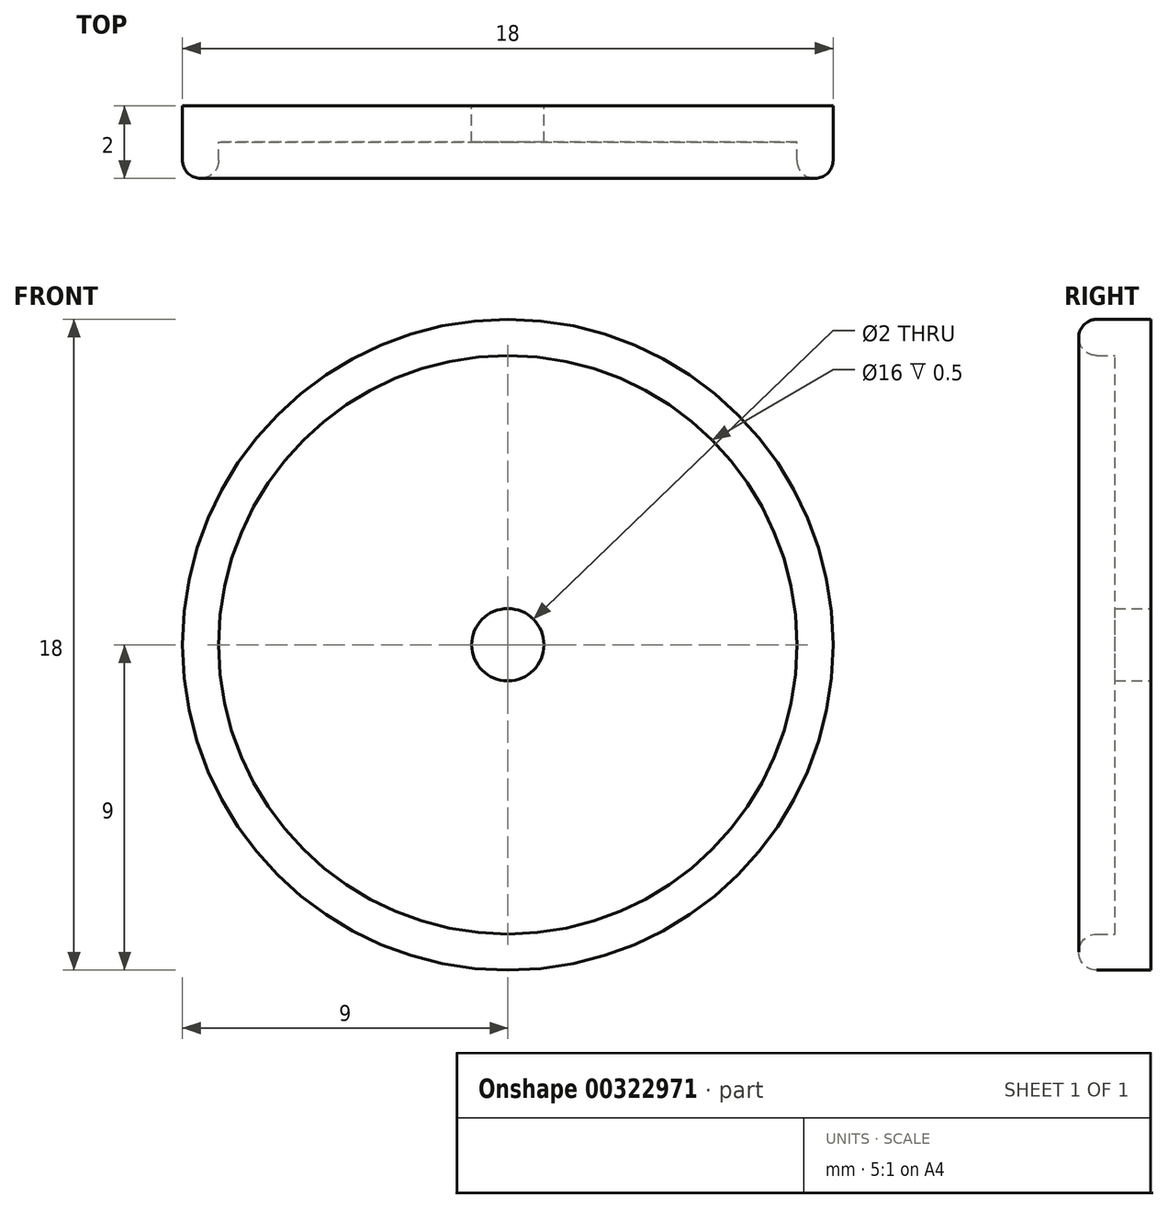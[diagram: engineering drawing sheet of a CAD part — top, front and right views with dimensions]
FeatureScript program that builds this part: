
annotation { "Feature Type Name" : "Feature", "Feature Type Description" : "" }
export const myFeature = defineFeature(function(context is Context, id is Id, definition is map)
    precondition{}
    {
        {
            var Q0;
            Q0=qCreatedBy(makeId("Front.planeOp"),FACE);
            var sketch = newSketch(context, id + "F0", { "sketchPlane" : qUnion([Q0])});
            skCircle(sketch, "E0", {"center": v(0, 0) * mm, "radius": 1 * mm});
            skCircle(sketch, "E1", {"center": v(0, 0) * mm, "radius": 9 * mm});
            skCircle(sketch, "E2", {"center": v(0, 0) * mm, "radius": 8 * mm});
            skSolve(sketch);
        }
        {
            var Q0;
            Q0=makeQuery(id+"F0.imprint","IMPRINT",FACE,{"disambiguationData":[TD([[makeQuery(id+"F0.imprint","IMPRINT",EDGE,{"derivedFrom":sQuery(id+"F0.wireOp",EDGE,"E0")}),-1.0]])]});
            extrude(context, id + "F1", {"entities" : qUnion([Q0]), "depth" : mm});
        }
        {
            var Q0;
            Q0 = qSketchRegion(id + "F0", true);
            extrude(context, id + "F2", {"entities" : qUnion([Q0]), "operationType" : NewBodyOperationType.ADD, "depth" : 2 * mm});
        }
        {
            var Q0;
            Q0=makeQuery(id+"F2.opExtrude","CAP_EDGE",EDGE,{"disambiguationData":[OSD([sQuery(id+"F0.wireOp",EDGE,"E1")])],"isStart":false});
            var Q1;
            Q1=makeQuery(id+"F2.opExtrude","CAP_EDGE",EDGE,{"disambiguationData":[OSD([sQuery(id+"F0.wireOp",EDGE,"E2")])],"isStart":false});
            fillet(context, id + "F3", {"entities" : qUnion([Q0, Q1]), "radius" : .5 * mm, "tangentPropagation" : true, "allowEdgeOverflow" : false});
        }
    });
